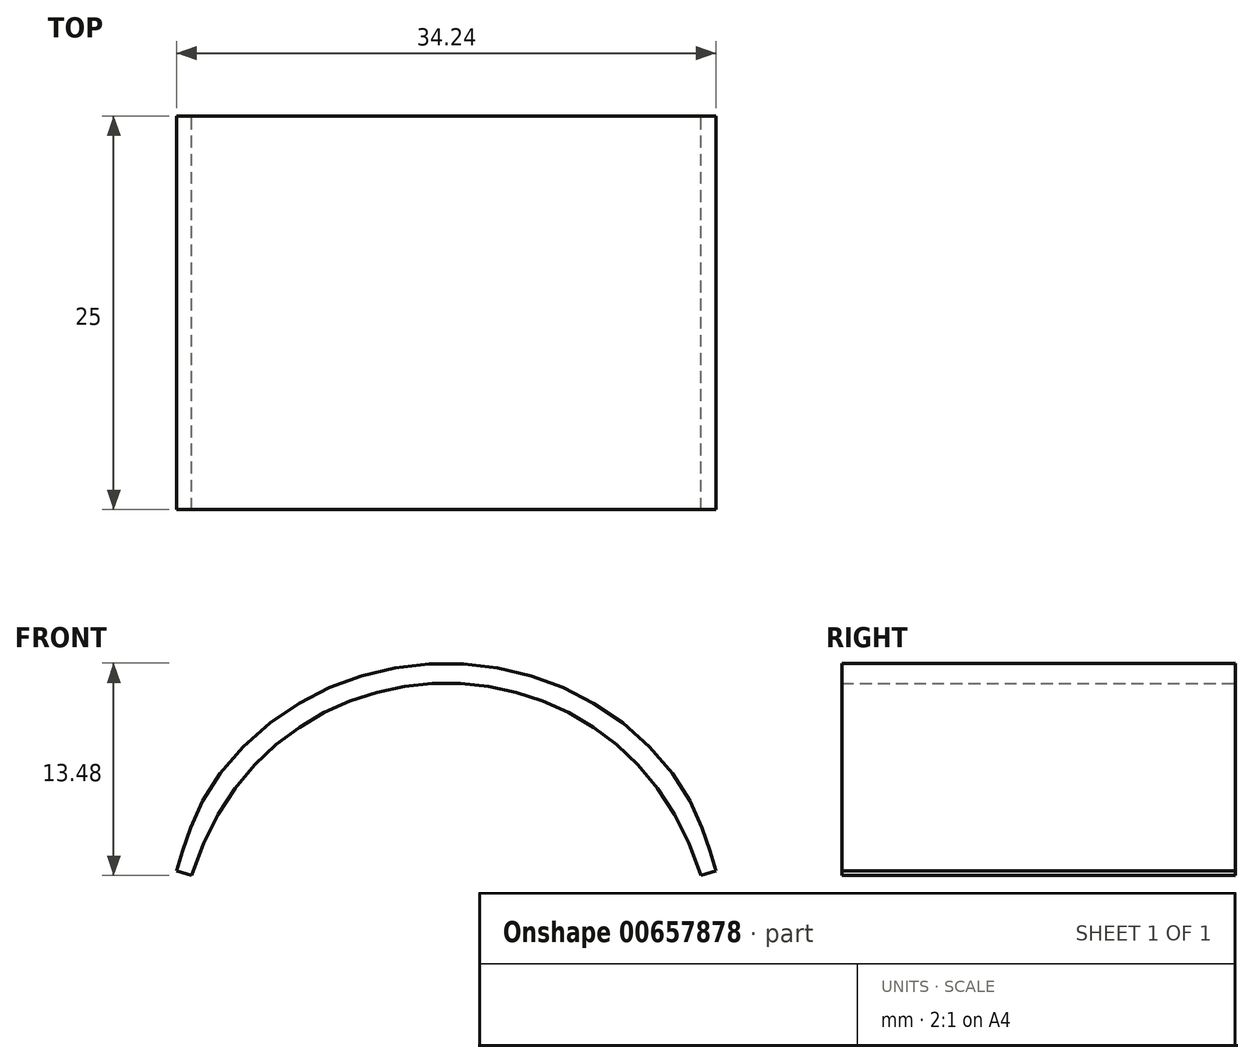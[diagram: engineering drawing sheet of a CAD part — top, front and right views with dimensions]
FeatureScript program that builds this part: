
annotation { "Feature Type Name" : "Feature", "Feature Type Description" : "" }
export const myFeature = defineFeature(function(context is Context, id is Id, definition is map)
    precondition{}
    {
        {
            var Q0;
            Q0=qCreatedBy(makeId("Front.planeOp"),FACE);
            var sketch = newSketch(context, id + "F0", { "sketchPlane" : qUnion([Q0])});
            skFitSpline(sketch, "E0", {"points": [v(-16.16, 0) * mm, v(16.16, 0) * mm], "startDerivative": vector(14.96, 48.83) * mm, "endDerivative": vector(14.96, -48.83) * mm});
            skFitSpline(sketch, "E1.0", {"points": [v(-17.12, 0.3) * mm, v(-16.47, 2.43) * mm, v(-14.58, 6.19) * mm, v(-10.43, 10.24) * mm, v(-5.42, 12.67) * mm, v(0, 13.48) * mm, v(5.42, 12.67) * mm, v(10.43, 10.24) * mm, v(14.58, 6.19) * mm, v(16.47, 2.43) * mm, v(17.12, 0.3) * mm]});
            skLineSegment(sketch, "E2", {"start": v(-17.12, 0.3) * mm, "end": v(-16.16, 0) * mm});
            skLineSegment(sketch, "E3", {"start": v(16.16, 0) * mm, "end": v(17.12, 0.3) * mm});
            skSolve(sketch);
        }
        {
            var Q0;
            Q0=makeQuery(id+"F0.imprint","IMPRINT",FACE,{"disambiguationData":[TD([[makeQuery(id+"F0.imprint","IMPRINT",EDGE,{"derivedFrom":sQuery(id+"F0.wireOp",EDGE,"E0")}),1.0]])]});
            extrude(context, id + "F1", {"entities" : qUnion([Q0]), "depth" : 25 * mm, "offsetDistance" : 25 * mm});
        }
    });
